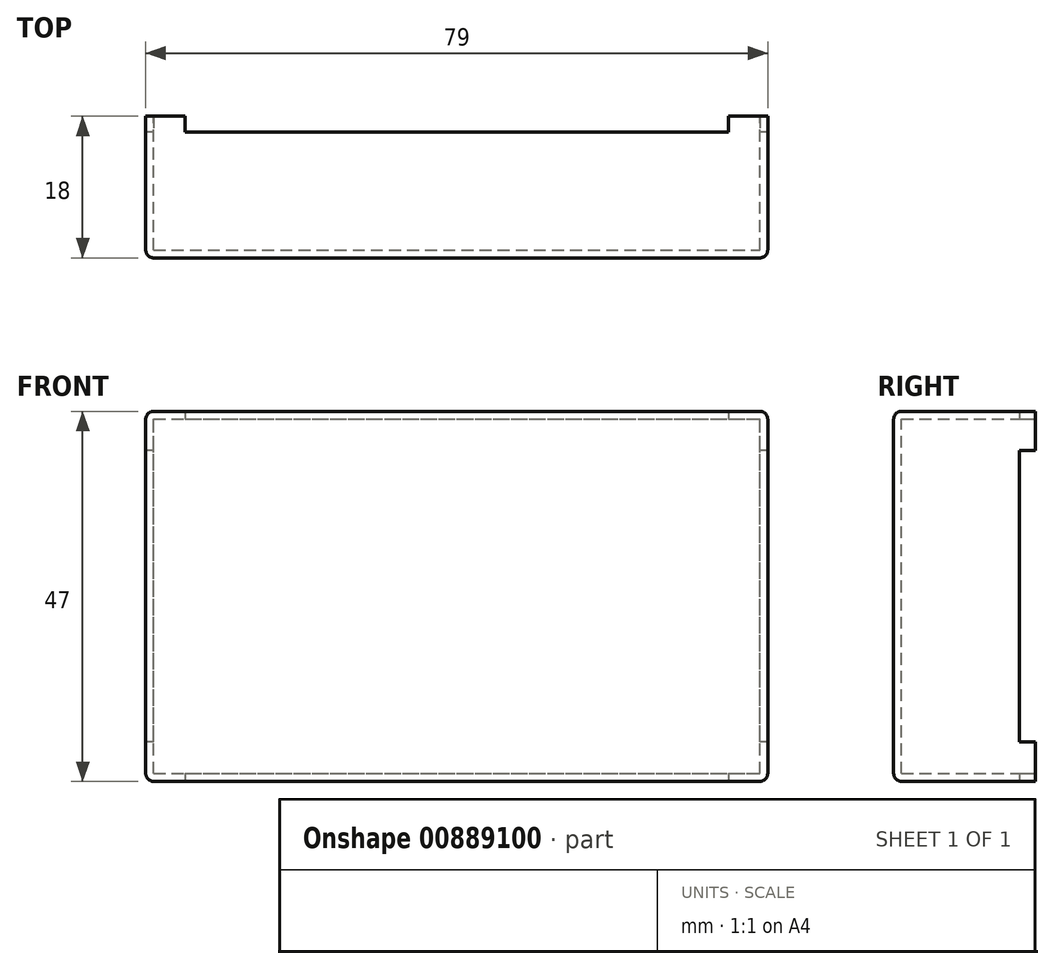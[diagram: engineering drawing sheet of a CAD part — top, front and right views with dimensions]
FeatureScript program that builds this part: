
annotation { "Feature Type Name" : "Feature", "Feature Type Description" : "" }
export const myFeature = defineFeature(function(context is Context, id is Id, definition is map)
    precondition{}
    {
        {
            var Q0;
            Q0=qCreatedBy(makeId("Front.planeOp"),FACE);
            var sketch = newSketch(context, id + "F0", { "sketchPlane" : qUnion([Q0])});
            skLineSegment(sketch, "E0.bottom", {"start": v(0, 0) * mm, "end": v(77, 0) * mm});
            skLineSegment(sketch, "E0.top", {"start": v(0, 45) * mm, "end": v(77, 45) * mm});
            skLineSegment(sketch, "E0.left", {"start": v(0, 0) * mm, "end": v(0, 45) * mm});
            skLineSegment(sketch, "E0.right", {"start": v(77, 0) * mm, "end": v(77, 45) * mm});
            skLineSegment(sketch, "E1.bottom", {"start": v(-1, -1) * mm, "end": v(78, -1) * mm});
            skLineSegment(sketch, "E1.top", {"start": v(-1, 46) * mm, "end": v(78, 46) * mm});
            skLineSegment(sketch, "E1.left", {"start": v(-1, -1) * mm, "end": v(-1, 46) * mm});
            skLineSegment(sketch, "E1.right", {"start": v(78, -1) * mm, "end": v(78, 46) * mm});
            skSolve(sketch);
        }
        {
            var Q0;
            Q0 = qSketchRegion(id + "F0", true);
            extrude(context, id + "F1", {"entities" : qUnion([Q0]), "depth" : 17 * mm, "offsetDistance" : 25 * mm});
        }
        {
            var Q0;
            Q0=makeQuery(id+"F1.opExtrude","CAP_FACE",FACE,{"disambiguationData":[OSD([sQuery(id+"F0.wireOp",EDGE,"E0.bottom"),sQuery(id+"F0.wireOp",EDGE,"E0.top"),sQuery(id+"F0.wireOp",EDGE,"E0.left"),sQuery(id+"F0.wireOp",EDGE,"E0.right"),sQuery(id+"F0.wireOp",EDGE,"E1.bottom"),sQuery(id+"F0.wireOp",EDGE,"E1.top"),sQuery(id+"F0.wireOp",EDGE,"E1.left"),sQuery(id+"F0.wireOp",EDGE,"E1.right")])],"isStart":false});
            var sketch = newSketch(context, id + "F2", { "sketchPlane" : qUnion([Q0])});
            skLineSegment(sketch, "E2.bottom", {"start": v(-1, 46) * mm, "end": v(78, 46) * mm});
            skLineSegment(sketch, "E2.top", {"start": v(-1, -1) * mm, "end": v(78, -1) * mm});
            skLineSegment(sketch, "E2.left", {"start": v(-1, 46) * mm, "end": v(-1, -1) * mm});
            skLineSegment(sketch, "E2.right", {"start": v(78, 46) * mm, "end": v(78, -1) * mm});
            skSolve(sketch);
        }
        {
            var Q0;
            Q0 = qSketchRegion(id + "F2", true);
            extrude(context, id + "F3", {"entities" : qUnion([Q0]), "operationType" : NewBodyOperationType.ADD, "depth" : 1 * mm, "offsetDistance" : 25 * mm});
        }
        {
            var Q0;
            Q0=makeQuery(id+"F3.boolean.opBoolean","MERGE",FACE,{"derivedFrom":[makeQuery(id+"F1.opExtrude","SWEPT_FACE",FACE,{"disambiguationData":[OSD([sQuery(id+"F0.wireOp",EDGE,"E1.left")])]}),makeQuery(id+"F3.opExtrude","SWEPT_FACE",FACE,{"disambiguationData":[OSD([sQuery(id+"F2.wireOp",EDGE,"E2.left")])]})]});
            var sketch = newSketch(context, id + "F4", { "sketchPlane" : qUnion([Q0])});
            skLineSegment(sketch, "E3.bottom", {"start": v(0, 4) * mm, "end": v(2, 4) * mm});
            skLineSegment(sketch, "E3.top", {"start": v(0, 41) * mm, "end": v(2, 41) * mm});
            skLineSegment(sketch, "E3.left", {"start": v(0, 4) * mm, "end": v(0, 41) * mm});
            skLineSegment(sketch, "E3.right", {"start": v(2, 4) * mm, "end": v(2, 41) * mm});
            skSolve(sketch);
        }
        {
            var Q0;
            Q0 = qSketchRegion(id + "F4", true);
            extrude(context, id + "F5", {"entities" : qUnion([Q0]), "operationType" : NewBodyOperationType.REMOVE, "endBound" : BoundingType.THROUGH_ALL, "oppositeDirection" : true, "depth" : 25 * mm, "offsetDistance" : 25 * mm});
        }
        {
            var Q0;
            Q0=makeQuery(id+"F3.boolean.opBoolean","MERGE",FACE,{"derivedFrom":[makeQuery(id+"F1.opExtrude","SWEPT_FACE",FACE,{"disambiguationData":[OSD([sQuery(id+"F0.wireOp",EDGE,"E1.bottom")])]}),makeQuery(id+"F3.opExtrude","SWEPT_FACE",FACE,{"disambiguationData":[OSD([sQuery(id+"F2.wireOp",EDGE,"E2.top")])]})]});
            var sketch = newSketch(context, id + "F6", { "sketchPlane" : qUnion([Q0])});
            skLineSegment(sketch, "E4.bottom", {"start": v(73, 0) * mm, "end": v(4, 0) * mm});
            skLineSegment(sketch, "E4.top", {"start": v(73, 2) * mm, "end": v(4, 2) * mm});
            skLineSegment(sketch, "E4.left", {"start": v(73, 0) * mm, "end": v(73, 2) * mm});
            skLineSegment(sketch, "E4.right", {"start": v(4, 0) * mm, "end": v(4, 2) * mm});
            skSolve(sketch);
        }
        {
            var Q0;
            Q0 = qSketchRegion(id + "F6", true);
            extrude(context, id + "F7", {"entities" : qUnion([Q0]), "operationType" : NewBodyOperationType.REMOVE, "endBound" : BoundingType.THROUGH_ALL, "oppositeDirection" : true, "depth" : 25 * mm, "offsetDistance" : 25 * mm});
        }
        {
            var Q0;
            Q0=makeQuery(id+"F3.opExtrude","CAP_FACE",FACE,{"disambiguationData":[OSD([sQuery(id+"F2.wireOp",EDGE,"E2.bottom"),sQuery(id+"F2.wireOp",EDGE,"E2.top"),sQuery(id+"F2.wireOp",EDGE,"E2.left"),sQuery(id+"F2.wireOp",EDGE,"E2.right")])],"isStart":false});
            fillet(context, id + "F8", {"entities" : qUnion([Q0]), "radius" : 1 * mm, "tangentPropagation" : true, "allowEdgeOverflow" : false});
        }
        {
            var Q0;
            Q0=makeQuery(id+"F3.boolean.opBoolean","MERGE",EDGE,{"derivedFrom":[makeQuery(id+"F1.opExtrude","SWEPT_EDGE",EDGE,{"disambiguationData":[OSD([sQuery(id+"F0.wireOp",EDGE,"E1.top"),sQuery(id+"F0.wireOp",EDGE,"E1.left")])]}),makeQuery(id+"F3.opExtrude","SWEPT_EDGE",EDGE,{"disambiguationData":[OSD([sQuery(id+"F2.wireOp",EDGE,"E2.bottom"),sQuery(id+"F2.wireOp",EDGE,"E2.left")])]})]});
            var Q1;
            Q1=makeQuery(id+"F3.boolean.opBoolean","MERGE",EDGE,{"derivedFrom":[makeQuery(id+"F1.opExtrude","SWEPT_EDGE",EDGE,{"disambiguationData":[OSD([sQuery(id+"F0.wireOp",EDGE,"E1.bottom"),sQuery(id+"F0.wireOp",EDGE,"E1.left")])]}),makeQuery(id+"F3.opExtrude","SWEPT_EDGE",EDGE,{"disambiguationData":[OSD([sQuery(id+"F2.wireOp",EDGE,"E2.top"),sQuery(id+"F2.wireOp",EDGE,"E2.left")])]})]});
            var Q2;
            Q2=makeQuery(id+"F3.boolean.opBoolean","MERGE",EDGE,{"derivedFrom":[makeQuery(id+"F1.opExtrude","SWEPT_EDGE",EDGE,{"disambiguationData":[OSD([sQuery(id+"F0.wireOp",EDGE,"E1.bottom"),sQuery(id+"F0.wireOp",EDGE,"E1.right")])]}),makeQuery(id+"F3.opExtrude","SWEPT_EDGE",EDGE,{"disambiguationData":[OSD([sQuery(id+"F2.wireOp",EDGE,"E2.top"),sQuery(id+"F2.wireOp",EDGE,"E2.right")])]})]});
            var Q3;
            Q3=makeQuery(id+"F3.boolean.opBoolean","MERGE",EDGE,{"derivedFrom":[makeQuery(id+"F1.opExtrude","SWEPT_EDGE",EDGE,{"disambiguationData":[OSD([sQuery(id+"F0.wireOp",EDGE,"E1.top"),sQuery(id+"F0.wireOp",EDGE,"E1.right")])]}),makeQuery(id+"F3.opExtrude","SWEPT_EDGE",EDGE,{"disambiguationData":[OSD([sQuery(id+"F2.wireOp",EDGE,"E2.bottom"),sQuery(id+"F2.wireOp",EDGE,"E2.right")])]})]});
            fillet(context, id + "F9", {"entities" : qUnion([Q0, Q1, Q2, Q3]), "radius" : 1 * mm, "tangentPropagation" : true, "allowEdgeOverflow" : false});
        }
    });
